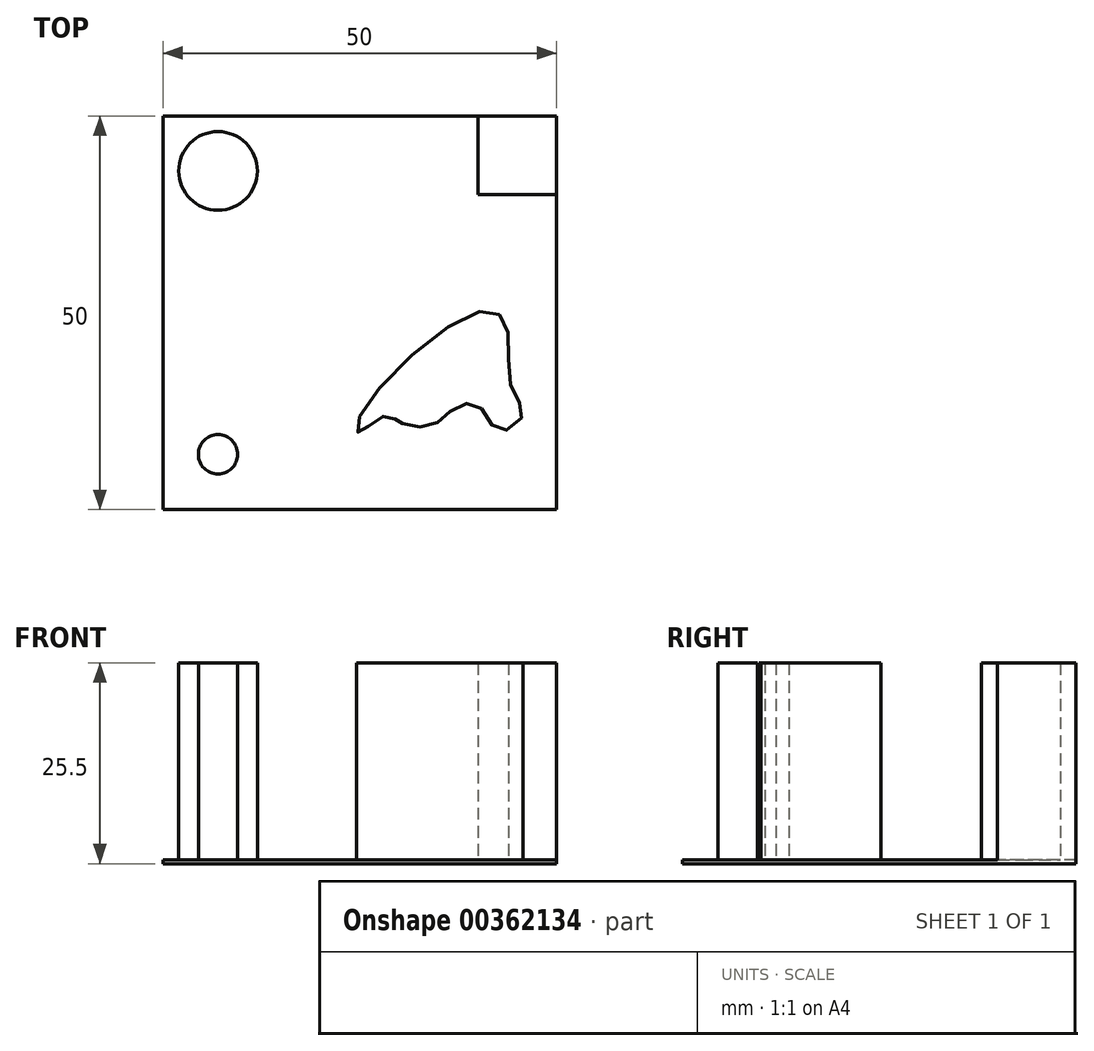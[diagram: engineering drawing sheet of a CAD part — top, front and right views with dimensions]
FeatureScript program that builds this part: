
annotation { "Feature Type Name" : "Feature", "Feature Type Description" : "" }
export const myFeature = defineFeature(function(context is Context, id is Id, definition is map)
    precondition{}
    {
        {
            var Q0;
            Q0=qCreatedBy(makeId("Top.planeOp"),FACE);
            var sketch = newSketch(context, id + "F0", { "sketchPlane" : qUnion([Q0])});
            skLineSegment(sketch, "E0.bottom", {"start": v(-25, 25) * mm, "end": v(25, 25) * mm});
            skLineSegment(sketch, "E0.top", {"start": v(-25, -25) * mm, "end": v(25, -25) * mm});
            skLineSegment(sketch, "E0.left", {"start": v(-25, 25) * mm, "end": v(-25, -25) * mm});
            skLineSegment(sketch, "E0.right", {"start": v(25, 25) * mm, "end": v(25, -25) * mm});
            skPoint(sketch, "E0.middle", {"position": v(0, 0) * mm});
            skSolve(sketch);
        }
        {
            var Q0;
            Q0=makeQuery(id+"F0.imprint","IMPRINT",FACE,{"disambiguationData":[TD([[makeQuery(id+"F0.imprint","IMPRINT",EDGE,{"derivedFrom":sQuery(id+"F0.wireOp",EDGE,"E0.bottom")}),-1.0]])]});
            extrude(context, id + "F1", {"entities" : qUnion([Q0]), "depth" : 0.5 * mm, "offsetDistance" : 25 * mm});
        }
        {
            var Q0;
            Q0=makeQuery(id+"F1.opExtrude","CAP_FACE",FACE,{"disambiguationData":[OSD([sQuery(id+"F0.wireOp",EDGE,"E0.bottom"),sQuery(id+"F0.wireOp",EDGE,"E0.top"),sQuery(id+"F0.wireOp",EDGE,"E0.left"),sQuery(id+"F0.wireOp",EDGE,"E0.right")])],"isStart":false});
            var sketch = newSketch(context, id + "F2", { "sketchPlane" : qUnion([Q0])});
            skCircle(sketch, "E1", {"center": v(-18, 18) * mm, "radius": 5 * mm});
            skCircle(sketch, "E2", {"center": v(-18, -18) * mm, "radius": 2.5 * mm});
            skLineSegment(sketch, "E3.bottom", {"start": v(15, 25) * mm, "end": v(25, 25) * mm});
            skLineSegment(sketch, "E3.top", {"start": v(15, 15) * mm, "end": v(25, 15) * mm});
            skLineSegment(sketch, "E3.left", {"start": v(15, 25) * mm, "end": v(15, 15) * mm});
            skLineSegment(sketch, "E3.right", {"start": v(25, 25) * mm, "end": v(25, 15) * mm});
            skPoint(sketch, "E3.middle", {"position": v(20, 20) * mm});
            skFitSpline(sketch, "E4", {"points": [v(0, -13.2) * mm, v(14.8, 0) * mm, v(18.6, -1.56) * mm, v(19.2, -9.45) * mm, v(20.68, -13) * mm, v(17.67, -15) * mm, v(15.06, -11.79) * mm, v(11.79, -12.32) * mm, v(8.98, -14.4) * mm, v(5.24, -14) * mm, v(4.57, -13.53) * mm, v(2.63, -13.26) * mm, v(0, -15.27) * mm, v(0, -13.2) * mm]});
            skSolve(sketch);
        }
        {
            var Q0;
            Q0=makeQuery(id+"F2.imprint","IMPRINT",FACE,{"disambiguationData":[TD([[makeQuery(id+"F2.imprint","IMPRINT",EDGE,{"derivedFrom":sQuery(id+"F2.wireOp",EDGE,"E1")}),1.0]])]});
            var Q1;
            Q1=makeQuery(id+"F2.imprint","IMPRINT",FACE,{"disambiguationData":[TD([[makeQuery(id+"F2.imprint","IMPRINT",EDGE,{"derivedFrom":sQuery(id+"F2.wireOp",EDGE,"E3.bottom")}),-1.0]])]});
            var Q2;
            Q2=makeQuery(id+"F2.imprint","IMPRINT",FACE,{"disambiguationData":[TD([[makeQuery(id+"F2.imprint","IMPRINT",EDGE,{"derivedFrom":sQuery(id+"F2.wireOp",EDGE,"E4")}),-1.0]])]});
            var Q3;
            Q3=makeQuery(id+"F2.imprint","IMPRINT",FACE,{"disambiguationData":[TD([[makeQuery(id+"F2.imprint","IMPRINT",EDGE,{"derivedFrom":sQuery(id+"F2.wireOp",EDGE,"E2")}),1.0]])]});
            extrude(context, id + "F3", {"entities" : qUnion([Q0, Q1, Q2, Q3]), "operationType" : NewBodyOperationType.ADD, "depth" : 25 * mm, "offsetDistance" : 25 * mm});
        }
    });
